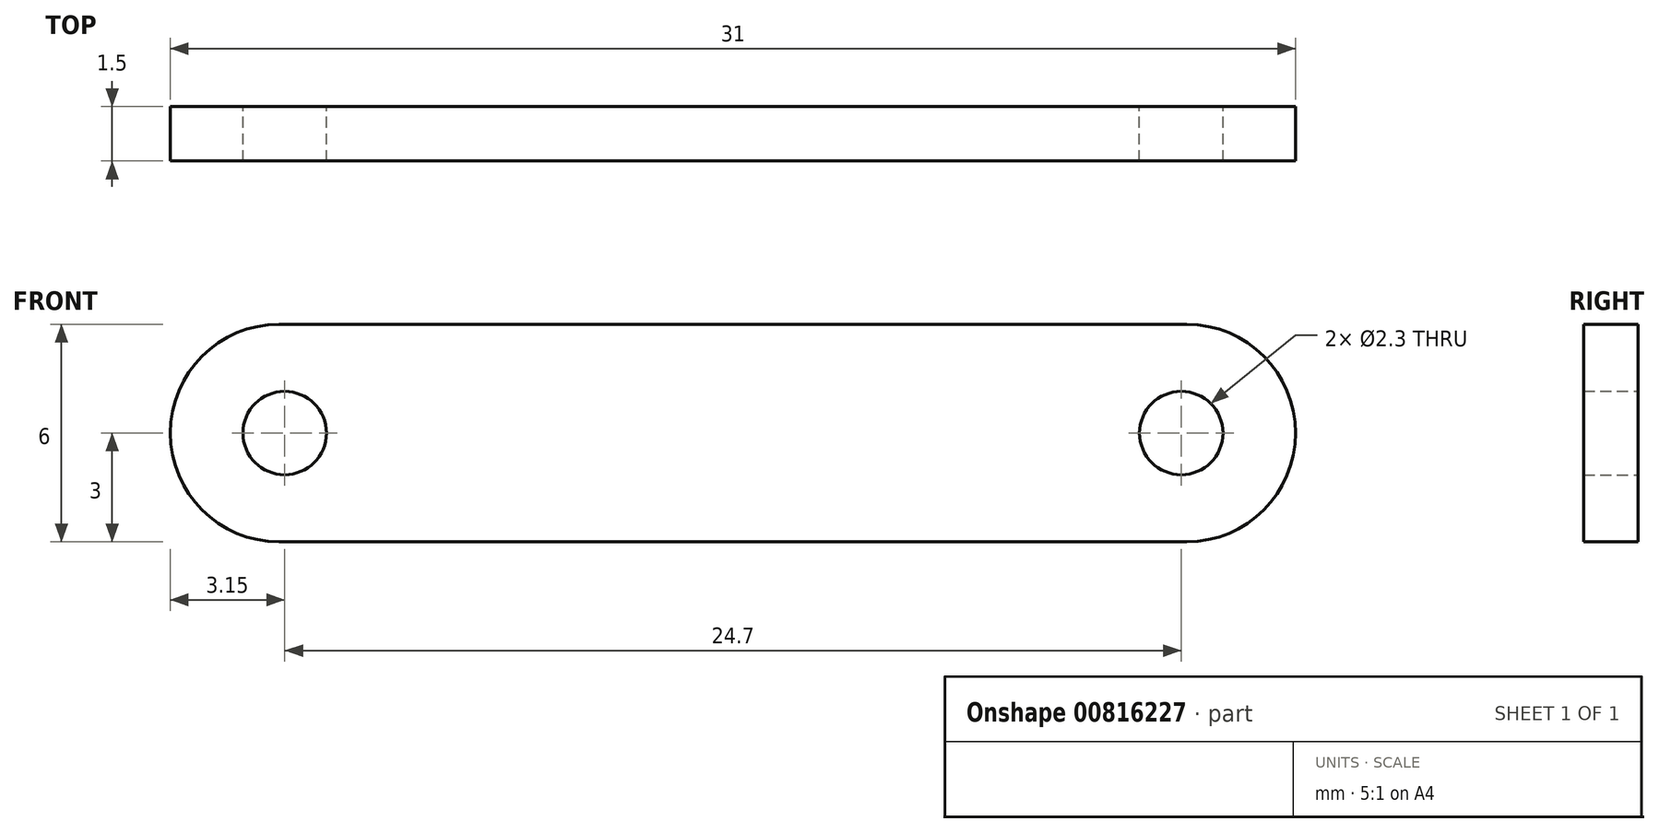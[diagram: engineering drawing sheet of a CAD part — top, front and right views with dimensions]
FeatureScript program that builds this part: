
annotation { "Feature Type Name" : "Feature", "Feature Type Description" : "" }
export const myFeature = defineFeature(function(context is Context, id is Id, definition is map)
    precondition{}
    {
        {
            var Q0;
            Q0=qCreatedBy(makeId("Front.planeOp"),FACE);
            var sketch = newSketch(context, id + "F0", { "sketchPlane" : qUnion([Q0])});
            skCircle(sketch, "E0", {"center": v(-12.35, 0) * mm, "radius": 1.15 * mm});
            skCircle(sketch, "E1", {"center": v(12.35, 0) * mm, "radius": 1.15 * mm});
            skLineSegment(sketch, "E2.bottom", {"start": v(-12.5, 3) * mm, "end": v(12.5, 3) * mm});
            skLineSegment(sketch, "E2.top", {"start": v(-12.5, -3) * mm, "end": v(12.5, -3) * mm});
            skLineSegment(sketch, "E2.left", {"start": v(-15.5, 0) * mm, "end": v(-15.5, 0) * mm});
            skLineSegment(sketch, "E2.right", {"start": v(15.5, 0) * mm, "end": v(15.5, 0) * mm});
            skPoint(sketch, "E3.visualSharp", {"position": v(15.5, 3) * mm});
            skArc(sketch, "E3.filletArc", {"start": v(15.5, 0) * mm, "mid": v(14.62, 2.12) * mm, "end": v(12.5, 3) * mm});
            skPoint(sketch, "E4.visualSharp", {"position": v(15.5, -3) * mm});
            skArc(sketch, "E4.filletArc", {"start": v(12.5, -3) * mm, "mid": v(14.62, -2.12) * mm, "end": v(15.5, 0) * mm});
            skPoint(sketch, "E5.visualSharp", {"position": v(-15.5, 3) * mm});
            skArc(sketch, "E5.filletArc", {"start": v(-12.5, 3) * mm, "mid": v(-14.62, 2.12) * mm, "end": v(-15.5, 0) * mm});
            skPoint(sketch, "E6.visualSharp", {"position": v(-15.5, -3) * mm});
            skArc(sketch, "E6.filletArc", {"start": v(-15.5, 0) * mm, "mid": v(-14.62, -2.12) * mm, "end": v(-12.5, -3) * mm});
            skSolve(sketch);
        }
        {
            var Q0;
            Q0=makeQuery(id+"F0.imprint","IMPRINT",FACE,{"disambiguationData":[TD([[makeQuery(id+"F0.imprint","IMPRINT",EDGE,{"derivedFrom":sQuery(id+"F0.wireOp",EDGE,"E0")}),-1.0]])]});
            extrude(context, id + "F1", {"entities" : qUnion([Q0]), "depth" : 1.5 * mm, "offsetDistance" : 25 * mm});
        }
    });
